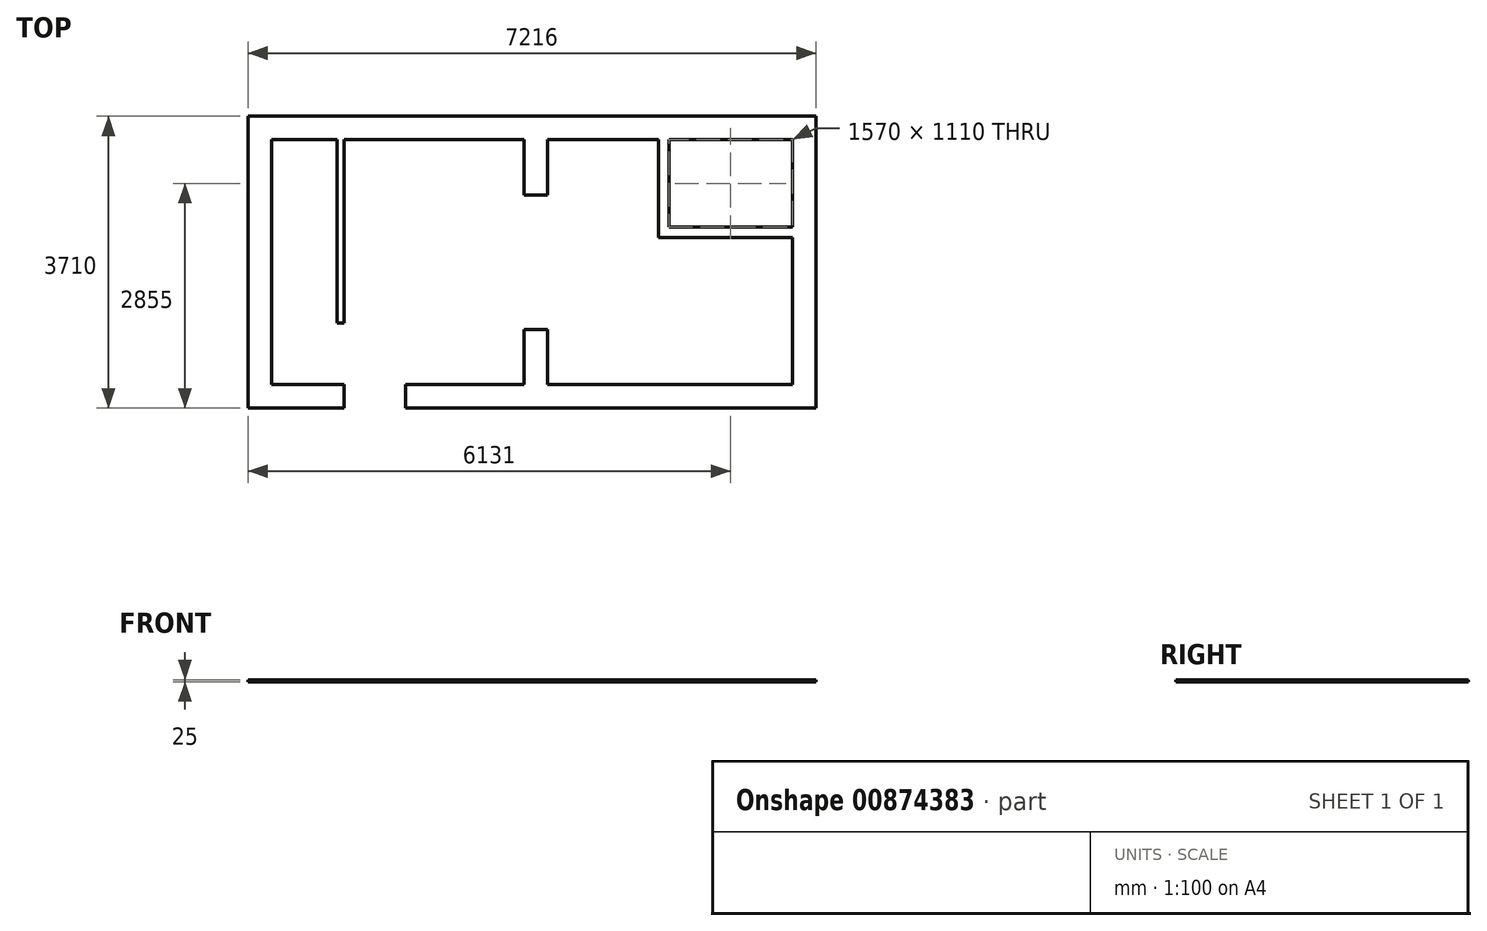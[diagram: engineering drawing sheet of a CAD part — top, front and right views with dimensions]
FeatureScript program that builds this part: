
annotation { "Feature Type Name" : "Feature", "Feature Type Description" : "" }
export const myFeature = defineFeature(function(context is Context, id is Id, definition is map)
    precondition{}
    {
        {
            var Q0;
            Q0=qCreatedBy(makeId("Top.planeOp"),FACE);
            var sketch = newSketch(context, id + "F0", { "sketchPlane" : qUnion([Q0])});
            skLineSegment(sketch, "E0", {"start": v(0, 0) * mm, "end": v(0, -1110) * mm});
            skLineSegment(sketch, "E1", {"start": v(0, -3110) * mm, "end": v(-3110, -3110) * mm});
            skLineSegment(sketch, "E2", {"start": v(-3110, -3110) * mm, "end": v(-3110, -2410) * mm});
            skLineSegment(sketch, "E3", {"start": v(-3110, -2410) * mm, "end": v(-3410, -2410) * mm});
            skLineSegment(sketch, "E4", {"start": v(-3410, -2410) * mm, "end": v(-3410, -3110) * mm});
            skLineSegment(sketch, "E5", {"start": v(-3410, -3110) * mm, "end": v(-4916, -3110) * mm});
            skLineSegment(sketch, "E6", {"start": v(-4916, -3110) * mm, "end": v(-4916, -3410) * mm});
            skLineSegment(sketch, "E7", {"start": v(-4916, -3410) * mm, "end": v(300, -3410) * mm});
            skLineSegment(sketch, "E8", {"start": v(300, -3410) * mm, "end": v(300, 300) * mm});
            skLineSegment(sketch, "E9", {"start": v(0, 0) * mm, "end": v(-1570, 0) * mm});
            skLineSegment(sketch, "E10", {"start": v(-3110, 0) * mm, "end": v(-3110, -700) * mm});
            skLineSegment(sketch, "E11", {"start": v(-3110, -700) * mm, "end": v(-3410, -700) * mm});
            skLineSegment(sketch, "E12", {"start": v(-3410, -700) * mm, "end": v(-3410, 0) * mm});
            skLineSegment(sketch, "E13", {"start": v(-1570, 0) * mm, "end": v(-1570, -1110) * mm});
            skLineSegment(sketch, "E14", {"start": v(-1570, -1110) * mm, "end": v(0, -1110) * mm});
            skLineSegment(sketch, "E15", {"start": v(-1700, 0) * mm, "end": v(-1700, -1240) * mm});
            skLineSegment(sketch, "E16", {"start": v(-1700, -1240) * mm, "end": v(0, -1240) * mm});
            skLineSegment(sketch, "E17.trimOffspring", {"start": v(-1700, 0) * mm, "end": v(-3110, 0) * mm});
            skLineSegment(sketch, "E18.trimOffspring", {"start": v(0, -1240) * mm, "end": v(0, -3110) * mm});
            skLineSegment(sketch, "E19", {"start": v(-5696, -3410) * mm, "end": v(-6916, -3410) * mm});
            skLineSegment(sketch, "E20", {"start": v(-6916, -3410) * mm, "end": v(-6916, 300) * mm});
            skLineSegment(sketch, "E21", {"start": v(-6916, 300) * mm, "end": v(300, 300) * mm});
            skLineSegment(sketch, "E22", {"start": v(-5696, -3410) * mm, "end": v(-5696, -3110) * mm});
            skLineSegment(sketch, "E23", {"start": v(-5696, -3110) * mm, "end": v(-6616, -3110) * mm});
            skLineSegment(sketch, "E24", {"start": v(-6616, -3110) * mm, "end": v(-6616, 0) * mm});
            skLineSegment(sketch, "E25", {"start": v(-6616, 0) * mm, "end": v(-5786, 0) * mm});
            skLineSegment(sketch, "E26", {"start": v(-5786, 0) * mm, "end": v(-5786, -2330) * mm});
            skLineSegment(sketch, "E27", {"start": v(-5786, -2330) * mm, "end": v(-5696, -2330) * mm});
            skLineSegment(sketch, "E28", {"start": v(-5696, -2330) * mm, "end": v(-5696, 0) * mm});
            skLineSegment(sketch, "E29", {"start": v(-5696, 0) * mm, "end": v(-3410, 0) * mm});
            skSolve(sketch);
        }
        {
            var Q0;
            Q0 = qSketchRegion(id + "F0", true);
            extrude(context, id + "F1", {"entities" : qUnion([Q0]), "depth" : 25 * mm, "offsetDistance" : 25 * mm});
        }
    });
